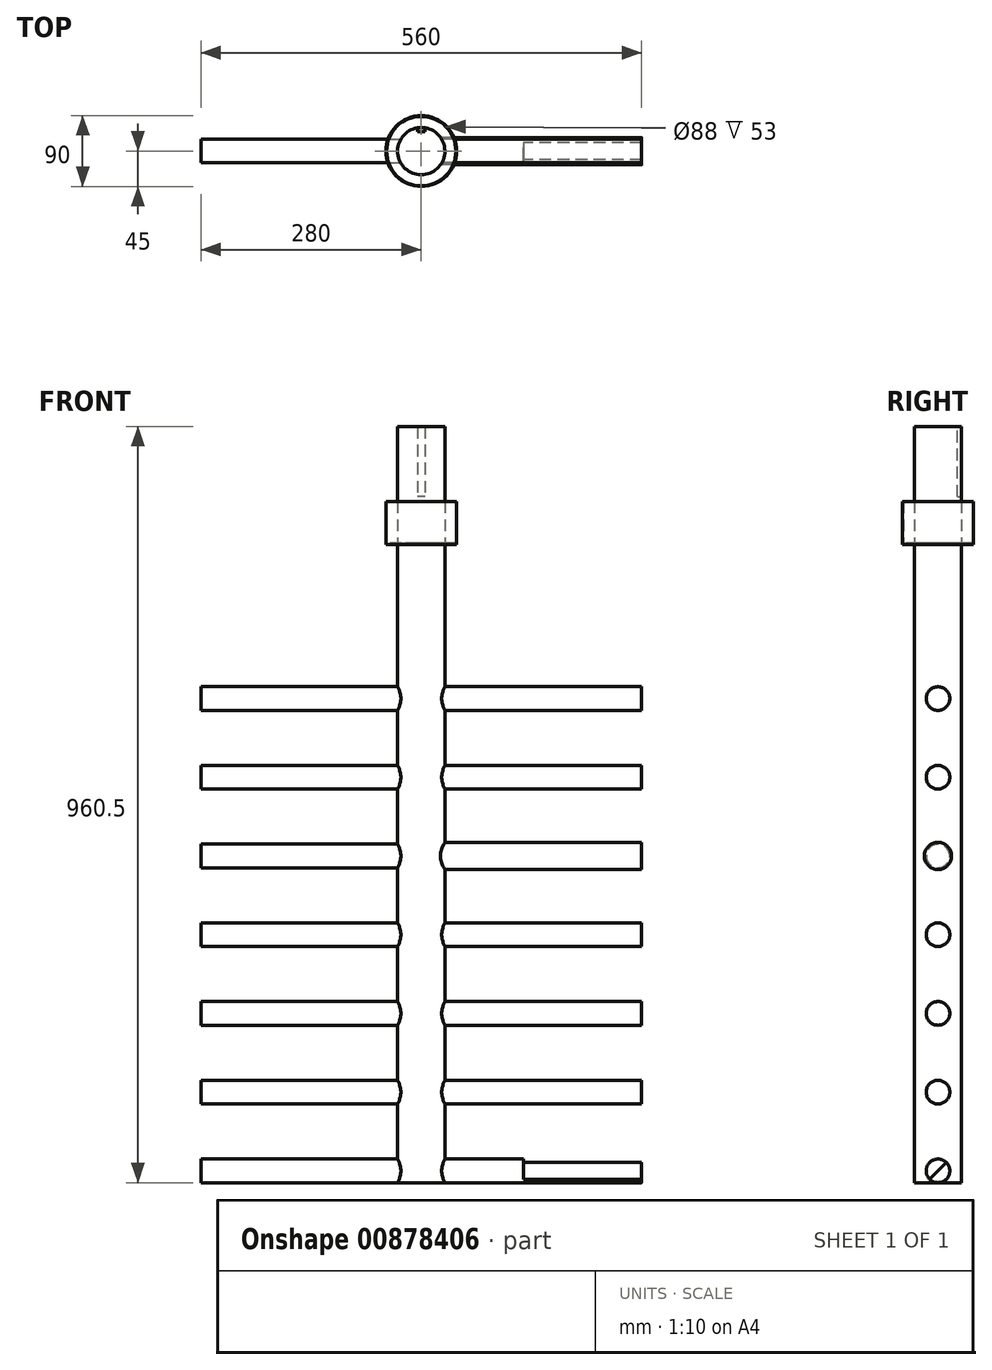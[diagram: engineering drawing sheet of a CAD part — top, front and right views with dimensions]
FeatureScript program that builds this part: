
annotation { "Feature Type Name" : "Feature", "Feature Type Description" : "" }
export const myFeature = defineFeature(function(context is Context, id is Id, definition is map)
    precondition{}
    {
        {
            var Q0;
            Q0=qCreatedBy(makeId("Top.planeOp"),FACE);
            var sketch = newSketch(context, id + "F0", { "sketchPlane" : qUnion([Q0])});
            skCircle(sketch, "E0", {"center": v(0, 0) * mm, "radius": 30 * mm});
            skSolve(sketch);
        }
        {
            var Q0;
            Q0 = qSketchRegion(id + "F0", true);
            extrude(context, id + "F1", {"entities" : qUnion([Q0]), "depth" : 960.5 * mm, "offsetDistance" : 25 * mm});
        }
        {
            var Q0;
            Q0=qCreatedBy(makeId("Right.planeOp"),FACE);
            var sketch = newSketch(context, id + "F2", { "sketchPlane" : qUnion([Q0])});
            skCircle(sketch, "E1", {"center": v(0, 15.02) * mm, "radius": 15 * mm});
            skCircle(sketch, "E2", {"center": v(0, 115.02) * mm, "radius": 15 * mm});
            skCircle(sketch, "E3", {"center": v(0, 215.02) * mm, "radius": 15 * mm});
            skCircle(sketch, "E4", {"center": v(0, 315.02) * mm, "radius": 15 * mm});
            skCircle(sketch, "E5", {"center": v(0, 415.02) * mm, "radius": 17.32 * mm});
            skCircle(sketch, "E6", {"center": v(0, 515.02) * mm, "radius": 15 * mm});
            skCircle(sketch, "E7", {"center": v(0, 615.02) * mm, "radius": 15 * mm});
            skSolve(sketch);
        }
        {
            var Q0;
            Q0 = qSketchRegion(id + "F2", true);
            extrude(context, id + "F3", {"entities" : qUnion([Q0]), "operationType" : NewBodyOperationType.ADD, "depth" : 280 * mm, "offsetDistance" : 25 * mm});
        }
        {
            var Q0;
            Q0=qCreatedBy(makeId("Right.planeOp"),FACE);
            var sketch = newSketch(context, id + "F4", { "sketchPlane" : qUnion([Q0])});
            skCircle(sketch, "E8", {"center": v(0, 15) * mm, "radius": 15 * mm});
            skCircle(sketch, "E9", {"center": v(0, 115) * mm, "radius": 15 * mm});
            skCircle(sketch, "E10", {"center": v(0, 215) * mm, "radius": 15 * mm});
            skCircle(sketch, "E11", {"center": v(0, 315) * mm, "radius": 15 * mm});
            skCircle(sketch, "E12", {"center": v(0, 415) * mm, "radius": 15 * mm});
            skCircle(sketch, "E13", {"center": v(0, 515) * mm, "radius": 15 * mm});
            skCircle(sketch, "E14", {"center": v(0, 615) * mm, "radius": 15 * mm});
            skSolve(sketch);
        }
        {
            var Q0;
            Q0 = qSketchRegion(id + "F4", true);
            extrude(context, id + "F5", {"entities" : qUnion([Q0]), "operationType" : NewBodyOperationType.ADD, "oppositeDirection" : true, "depth" : 280 * mm, "offsetDistance" : 25 * mm});
        }
        {
            var Q0;
            Q0=makeQuery(id+"F3.opExtrude","CAP_FACE",FACE,{"disambiguationData":[OSD([sQuery(id+"F2.wireOp",EDGE,"E1")])],"isStart":false});
            var sketch = newSketch(context, id + "F6", { "sketchPlane" : qUnion([Q0])});
            skLineSegment(sketch, "E15", {"start": v(-21.86, -6.84) * mm, "end": v(26.75, 41.77) * mm});
            skPoint(sketch, "E16.orphan", {"position": v(0, 15.02) * mm});
            skLineSegment(sketch, "E17", {"start": v(0, 15.02) * mm, "end": v(52.62, 15.02) * mm});
            skLineSegment(sketch, "E18", {"start": v(26.75, 41.77) * mm, "end": v(-25.04, 41.77) * mm});
            skLineSegment(sketch, "E19", {"start": v(-25.04, 41.77) * mm, "end": v(-21.86, -6.84) * mm});
            skSolve(sketch);
        }
        {
            var Q0;
            Q0 = qSketchRegion(id + "F6", true);
            extrude(context, id + "F7", {"entities" : qUnion([Q0]), "operationType" : NewBodyOperationType.REMOVE, "oppositeDirection" : true, "depth" : 150 * mm, "offsetDistance" : 25 * mm});
        }
        {
            var Q0;
            Q0=makeQuery(id+"F1.opExtrude","CAP_FACE",FACE,{"disambiguationData":[OSD([sQuery(id+"F0.wireOp",EDGE,"E0")])],"isStart":false});
            cPlane(context, id + "F8", {"entities" : qUnion([Q0]), "cplaneType" : CPlaneType.OFFSET, "offset" : 0 * mm, "width" : 150 * mm, "height" : 150 * mm});
        }
        {
            var Q0;
            Q0=makeQuery(id+"F1.opExtrude","CAP_FACE",FACE,{"disambiguationData":[OSD([sQuery(id+"F0.wireOp",EDGE,"E0")])],"isStart":false});
            cPlane(context, id + "F9", {"entities" : qUnion([Q0]), "cplaneType" : CPlaneType.OFFSET, "offset" : 150 * mm, "oppositeDirection" : true, "width" : 150 * mm, "height" : 150 * mm});
        }
        {
            var Q0;
            Q0=qCreatedBy(id+"F9.planeOp",FACE);
            var sketch = newSketch(context, id + "F10", { "sketchPlane" : qUnion([Q0])});
            skCircle(sketch, "E20", {"center": v(0, 0) * mm, "radius": 45 * mm});
            skSolve(sketch);
        }
        {
            var Q0;
            Q0=makeQuery(id+"F10.imprint","IMPRINT",FACE,{"disambiguationData":[TD([[makeQuery(id+"F10.imprint","IMPRINT",EDGE,{"derivedFrom":sQuery(id+"F10.wireOp",EDGE,"E20")}),1.0]])]});
            extrude(context, id + "F11", {"entities" : qUnion([Q0]), "operationType" : NewBodyOperationType.ADD, "depth" : 2 * mm, "offsetDistance" : 25 * mm});
        }
        {
            var Q0;
            Q0=qCreatedBy(id+"F9.planeOp",FACE);
            var sketch = newSketch(context, id + "F12", { "sketchPlane" : qUnion([Q0])});
            skCircle(sketch, "E21", {"center": v(0, 0) * mm, "radius": 45 * mm});
            skCircle(sketch, "E22", {"center": v(0, 0) * mm, "radius": 44 * mm});
            skSolve(sketch);
        }
        {
            var Q0;
            Q0 = qSketchRegion(id + "F12", true);
            extrude(context, id + "F13", {"entities" : qUnion([Q0]), "operationType" : NewBodyOperationType.ADD, "depth" : 55 * mm, "offsetDistance" : 25 * mm});
        }
        {
            var Q0;
            Q0=qCreatedBy(id+"F8.planeOp",FACE);
            var sketch = newSketch(context, id + "F14", { "sketchPlane" : qUnion([Q0])});
            skLineSegment(sketch, "E23.bottom", {"start": v(5, 24.74) * mm, "end": v(-5, 24.74) * mm});
            skLineSegment(sketch, "E23.top", {"start": v(5, 35.26) * mm, "end": v(-5, 35.26) * mm});
            skLineSegment(sketch, "E23.left", {"start": v(5, 24.74) * mm, "end": v(5, 35.26) * mm});
            skLineSegment(sketch, "E23.right", {"start": v(-5, 24.74) * mm, "end": v(-5, 35.26) * mm});
            skPoint(sketch, "E23.middle", {"position": v(0, 30) * mm});
            skSolve(sketch);
        }
        {
            var Q0;
            Q0=makeQuery(id+"F14.imprint","IMPRINT",FACE,{"disambiguationData":[TD([[makeQuery(id+"F14.imprint","IMPRINT",EDGE,{"derivedFrom":sQuery(id+"F14.wireOp",EDGE,"E23.bottom")}),-1.0]])]});
            extrude(context, id + "F15", {"entities" : qUnion([Q0]), "operationType" : NewBodyOperationType.REMOVE, "oppositeDirection" : true, "depth" : 89 * mm, "offsetDistance" : 25 * mm});
        }
    });
